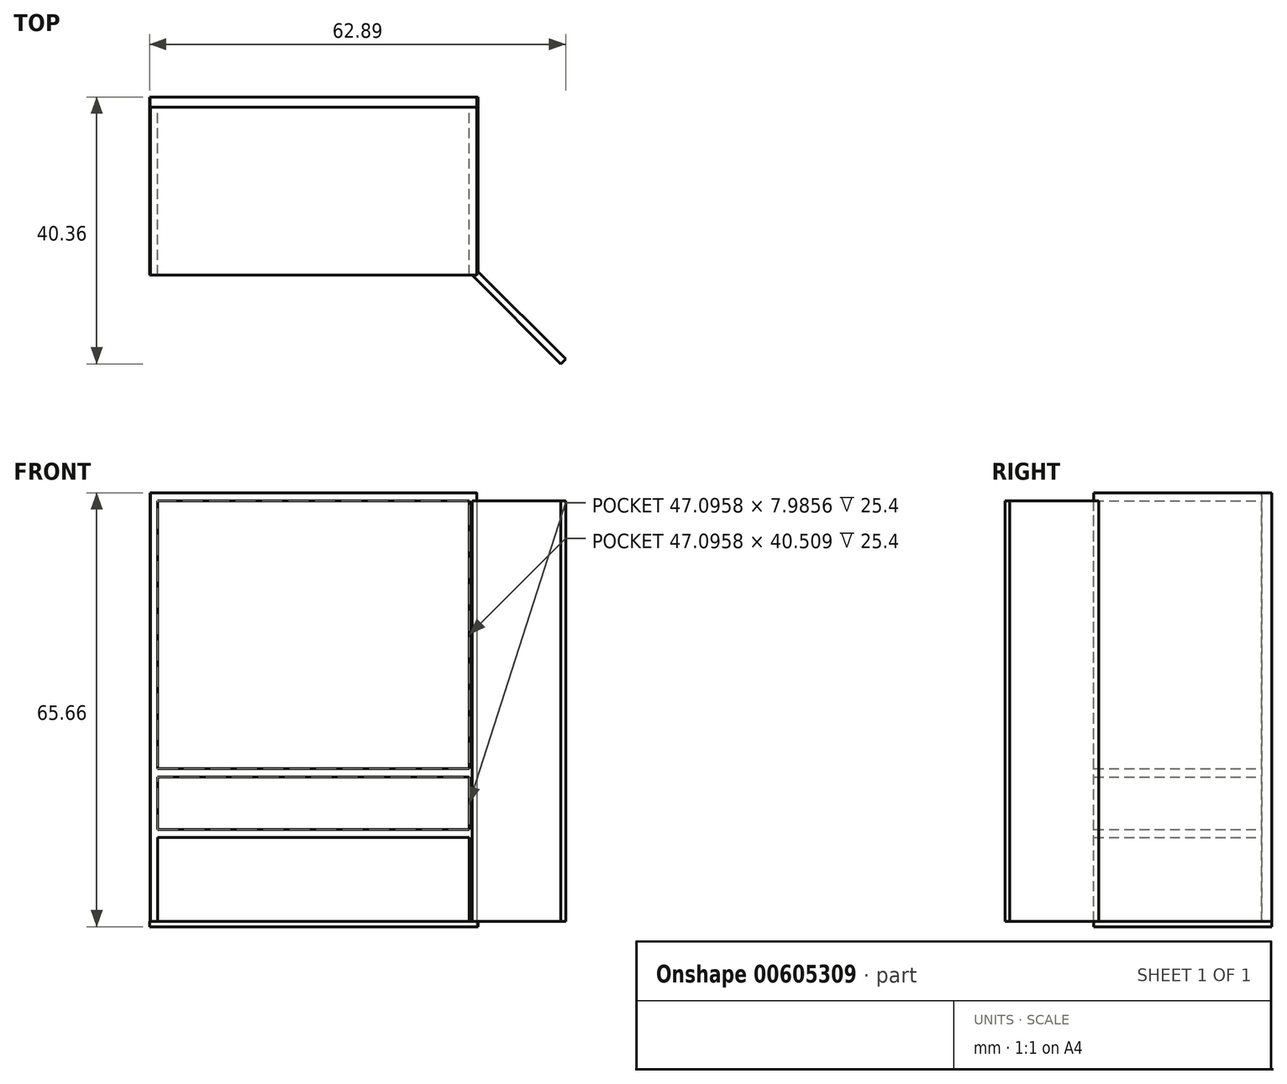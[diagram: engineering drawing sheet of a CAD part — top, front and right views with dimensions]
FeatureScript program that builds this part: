
annotation { "Feature Type Name" : "Feature", "Feature Type Description" : "" }
export const myFeature = defineFeature(function(context is Context, id is Id, definition is map)
    precondition{}
    {
        {
            var Q0;
            Q0=qCreatedBy(makeId("Front.planeOp"),FACE);
            var sketch = newSketch(context, id + "F0", { "sketchPlane" : qUnion([Q0])});
            skLineSegment(sketch, "E0.bottom", {"start": v(-24.68, 0) * mm, "end": v(-23.55, 0) * mm});
            skLineSegment(sketch, "E0.top", {"start": v(-24.68, 64.45) * mm, "end": v(-23.55, 64.45) * mm});
            skLineSegment(sketch, "E0.left", {"start": v(-24.68, 0) * mm, "end": v(-24.68, 64.45) * mm});
            skLineSegment(sketch, "E0.right", {"start": v(-23.55, 0) * mm, "end": v(-23.55, 64.45) * mm});
            skLineSegment(sketch, "E1", {"start": v(0, 76.3) * mm, "end": v(0, 0) * mm, "construction": true});
            skLineSegment(sketch, "E2.MirrorCS", {"start": v(23.55, 0) * mm, "end": v(23.55, 64.45) * mm});
            skLineSegment(sketch, "E3.MirrorCS", {"start": v(24.68, 0) * mm, "end": v(24.68, 64.45) * mm});
            skLineSegment(sketch, "E4.MirrorCS", {"start": v(24.68, 0) * mm, "end": v(23.55, 0) * mm});
            skLineSegment(sketch, "E5.MirrorCS", {"start": v(24.68, 64.45) * mm, "end": v(23.55, 64.45) * mm});
            skLineSegment(sketch, "E6.bottom", {"start": v(-24.68, 64.45) * mm, "end": v(24.68, 64.45) * mm});
            skLineSegment(sketch, "E6.top", {"start": v(-24.68, 65.64) * mm, "end": v(24.68, 65.64) * mm});
            skLineSegment(sketch, "E6.left", {"start": v(-24.68, 64.45) * mm, "end": v(-24.68, 65.64) * mm});
            skLineSegment(sketch, "E6.right", {"start": v(24.68, 64.45) * mm, "end": v(24.68, 65.64) * mm});
            skLineSegment(sketch, "E7.bottom", {"start": v(23.55, 23.94) * mm, "end": v(-23.55, 23.94) * mm});
            skLineSegment(sketch, "E7.top", {"start": v(23.55, 22.66) * mm, "end": v(-23.55, 22.66) * mm});
            skLineSegment(sketch, "E7.left", {"start": v(23.55, 23.94) * mm, "end": v(23.55, 22.66) * mm});
            skLineSegment(sketch, "E7.right", {"start": v(-23.55, 23.94) * mm, "end": v(-23.55, 22.66) * mm});
            skLineSegment(sketch, "E8.bottom", {"start": v(23.55, 14.68) * mm, "end": v(-23.55, 14.68) * mm});
            skLineSegment(sketch, "E8.top", {"start": v(23.55, 13.5) * mm, "end": v(-23.55, 13.5) * mm});
            skLineSegment(sketch, "E8.left", {"start": v(23.55, 14.68) * mm, "end": v(23.55, 13.5) * mm});
            skLineSegment(sketch, "E8.right", {"start": v(-23.55, 14.68) * mm, "end": v(-23.55, 13.5) * mm});
            skSolve(sketch);
        }
        {
            var Q0;
            Q0 = qSketchRegion(id + "F0", true);
            extrude(context, id + "F1", {"entities" : qUnion([Q0]), "depth" : 25.4 * mm, "offsetDistance" : 25.4 * mm});
        }
        {
            var Q0;
            Q0=makeQuery(id+"F0.imprint","IMPRINT",FACE,{"disambiguationData":[TD([[makeQuery(id+"F0.imprint","IMPRINT",EDGE,{"derivedFrom":sQuery(id+"F0.wireOp",EDGE,"E7.bottom")}),1.0]])]});
            extrude(context, id + "F2", {"entities" : qUnion([Q0]), "operationType" : NewBodyOperationType.ADD, "depth" : 25.4 * mm, "offsetDistance" : 25.4 * mm});
        }
        {
            var Q0;
            Q0=qCreatedBy(makeId("Front.planeOp"),FACE);
            var sketch = newSketch(context, id + "F3", { "sketchPlane" : qUnion([Q0])});
            skLineSegment(sketch, "E9.bottom", {"start": v(24.68, 65.66) * mm, "end": v(-24.74, 65.66) * mm});
            skLineSegment(sketch, "E9.top", {"start": v(24.68, 0) * mm, "end": v(-24.74, 0) * mm});
            skLineSegment(sketch, "E9.left", {"start": v(24.68, 65.66) * mm, "end": v(24.68, 0) * mm});
            skLineSegment(sketch, "E9.right", {"start": v(-24.74, 65.66) * mm, "end": v(-24.74, 0) * mm});
            skSolve(sketch);
        }
        {
            var Q0;
            Q0=makeQuery(id+"F3.imprint","IMPRINT",FACE,{"disambiguationData":[TD([[makeQuery(id+"F3.imprint","IMPRINT",EDGE,{"derivedFrom":sQuery(id+"F3.wireOp",EDGE,"E9.bottom")}),1.0]])]});
            extrude(context, id + "F4", {"entities" : qUnion([Q0]), "operationType" : NewBodyOperationType.ADD, "oppositeDirection" : true, "depth" : 1.52 * mm, "offsetDistance" : 25.4 * mm});
        }
        {
            var Q0;
            Q0=qCreatedBy(makeId("Top.planeOp"),FACE);
            var sketch = newSketch(context, id + "F5", { "sketchPlane" : qUnion([Q0])});
            skLineSegment(sketch, "E10.bottom", {"start": v(24.86, -25.42) * mm, "end": v(-24.77, -25.42) * mm});
            skLineSegment(sketch, "E10.top", {"start": v(24.86, 1.5) * mm, "end": v(-24.77, 1.5) * mm});
            skLineSegment(sketch, "E10.left", {"start": v(24.86, -25.42) * mm, "end": v(24.86, 1.5) * mm});
            skLineSegment(sketch, "E10.right", {"start": v(-24.77, -25.42) * mm, "end": v(-24.77, 1.5) * mm});
            skSolve(sketch);
        }
        {
            var Q0;
            Q0=makeQuery(id+"F5.imprint","IMPRINT",FACE,{"disambiguationData":[TD([[makeQuery(id+"F5.imprint","IMPRINT",EDGE,{"derivedFrom":sQuery(id+"F5.wireOp",EDGE,"E10.bottom")}),-1.0]])]});
            extrude(context, id + "F6", {"entities" : qUnion([Q0]), "operationType" : NewBodyOperationType.ADD, "depth" : 0.79 * mm, "offsetDistance" : 25.4 * mm});
        }
        {
            var Q0;
            Q0=sQuery(id+"F0.wireOp",EDGE,"E1");
            var Q1;
            Q1=qCreatedBy(makeId("Front.planeOp"),FACE);
            cPlane(context, id + "F7", {"entities" : qUnion([Q0, Q1]), "cplaneType" : CPlaneType.LINE_ANGLE, "offset" : 1143 * mm, "angle" : 45 * degree, "width" : 152.4 * mm, "height" : 152.4 * mm});
        }
        {
            var Q0;
            Q0=qCreatedBy(id+"F7.planeOp",FACE);
            var sketch = newSketch(context, id + "F8", { "sketchPlane" : qUnion([Q0])});
            skLineSegment(sketch, "E11.bottom", {"start": v(-34.66, 64.46) * mm, "end": v(-53.91, 64.46) * mm});
            skLineSegment(sketch, "E11.top", {"start": v(-34.66, 0.83) * mm, "end": v(-53.91, 0.83) * mm});
            skLineSegment(sketch, "E11.left", {"start": v(-34.66, 64.46) * mm, "end": v(-34.66, 0.83) * mm});
            skLineSegment(sketch, "E11.right", {"start": v(-53.91, 64.46) * mm, "end": v(-53.91, 0.83) * mm});
            skSolve(sketch);
        }
        {
            var Q0;
            Q0 = qSketchRegion(id + "F8", true);
            extrude(context, id + "F9", {"entities" : qUnion([Q0]), "operationType" : NewBodyOperationType.ADD, "oppositeDirection" : true, "depth" : 1.02 * mm, "offsetDistance" : 25.4 * mm});
        }
    });
